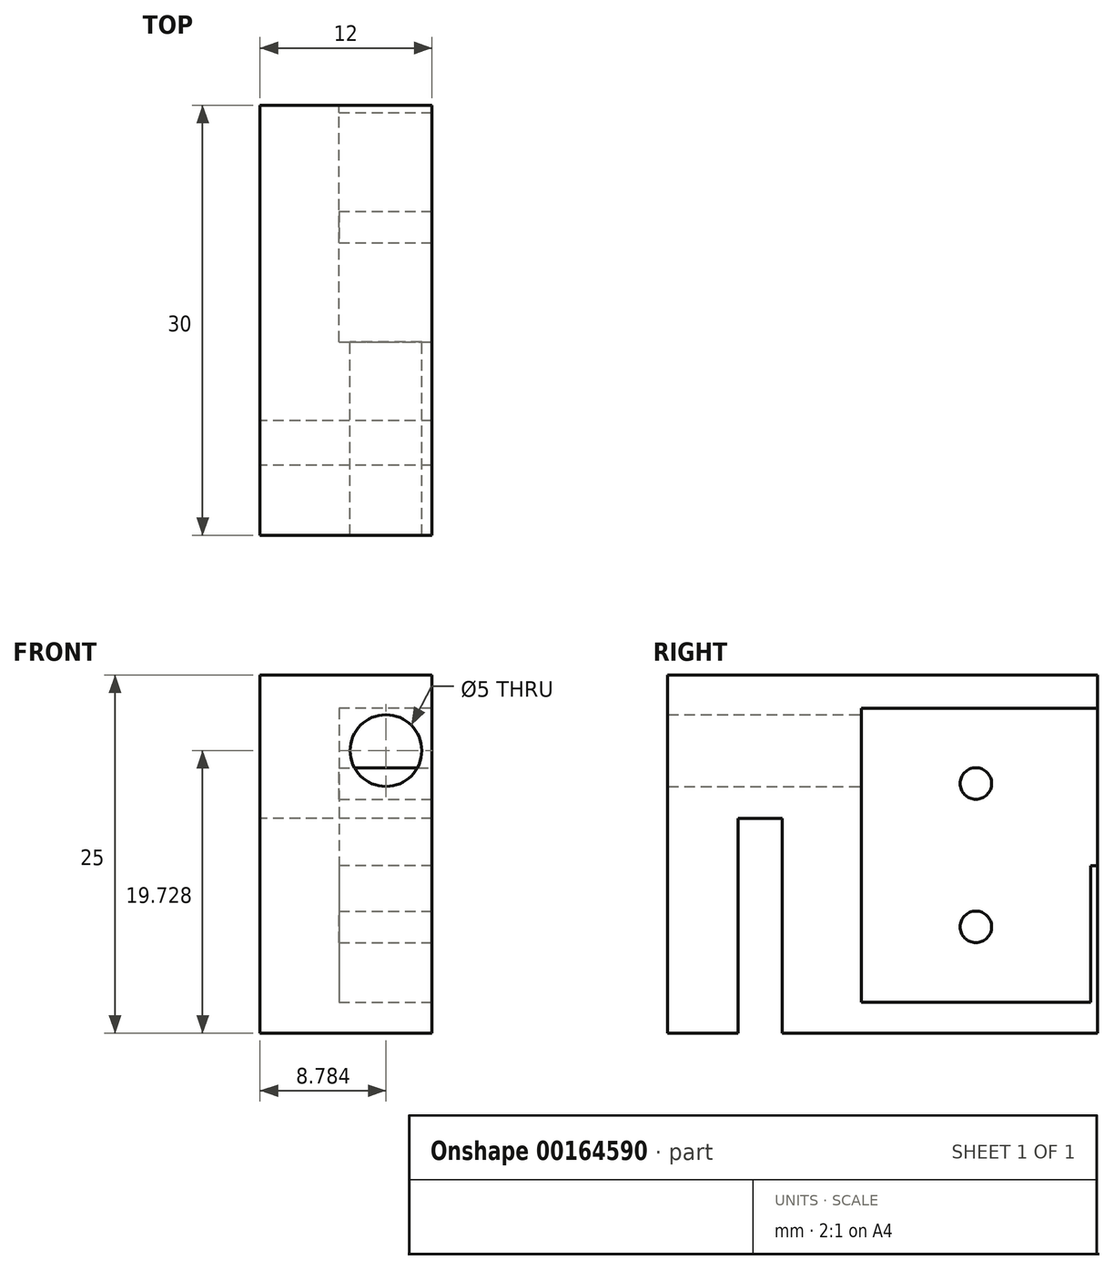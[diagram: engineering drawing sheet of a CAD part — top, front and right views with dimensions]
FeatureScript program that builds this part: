
annotation { "Feature Type Name" : "Feature", "Feature Type Description" : "" }
export const myFeature = defineFeature(function(context is Context, id is Id, definition is map)
    precondition{}
    {
        {
            var Q0;
            Q0=qCreatedBy(makeId("Right.planeOp"),FACE);
            var sketch = newSketch(context, id + "F0", { "sketchPlane" : qUnion([Q0])});
            skLineSegment(sketch, "E0.bottom", {"start": v(-4.9, -0.08) * mm, "end": v(25.1, -0.08) * mm});
            skLineSegment(sketch, "E0.top", {"start": v(-4.9, -25.08) * mm, "end": v(25.1, -25.08) * mm});
            skLineSegment(sketch, "E0.left", {"start": v(-4.9, -0.08) * mm, "end": v(-4.9, -25.08) * mm});
            skLineSegment(sketch, "E0.right", {"start": v(25.1, -0.08) * mm, "end": v(25.1, -25.08) * mm});
            skLineSegment(sketch, "E1.bottom", {"start": v(0, -25.08) * mm, "end": v(3.1, -25.08) * mm});
            skLineSegment(sketch, "E1.top", {"start": v(0, -10.08) * mm, "end": v(3.1, -10.08) * mm});
            skLineSegment(sketch, "E1.left", {"start": v(0, -25.08) * mm, "end": v(0, -10.08) * mm});
            skLineSegment(sketch, "E1.right", {"start": v(3.1, -25.08) * mm, "end": v(3.1, -10.08) * mm});
            skSolve(sketch);
        }
        {
            var Q0;
            Q0=makeQuery(id+"F0.imprint","IMPRINT",FACE,{"disambiguationData":[TD([[makeQuery(id+"F0.imprint","IMPRINT",EDGE,{"derivedFrom":sQuery(id+"F0.wireOp",EDGE,"E0.bottom")}),-1.0]])]});
            extrude(context, id + "F1", {"entities" : qUnion([Q0]), "depth" : 12 * mm});
        }
        {
            var Q0;
            Q0=makeQuery(id+"F1.opExtrude","CAP_FACE",FACE,{"disambiguationData":[OSD([sQuery(id+"F0.wireOp",EDGE,"E0.bottom"),sQuery(id+"F0.wireOp",EDGE,"E0.top"),sQuery(id+"F0.wireOp",EDGE,"E0.left"),sQuery(id+"F0.wireOp",EDGE,"E0.right"),sQuery(id+"F0.wireOp",EDGE,"E1.top"),sQuery(id+"F0.wireOp",EDGE,"E1.left"),sQuery(id+"F0.wireOp",EDGE,"E1.right")])],"isStart":false});
            var sketch = newSketch(context, id + "F2", { "sketchPlane" : qUnion([Q0])});
            skLineSegment(sketch, "E2.bottom", {"start": v(8.6, -2.4) * mm, "end": v(24.6, -2.4) * mm});
            skLineSegment(sketch, "E2.top", {"start": v(8.6, -22.9) * mm, "end": v(24.6, -22.9) * mm});
            skLineSegment(sketch, "E2.left", {"start": v(8.6, -2.4) * mm, "end": v(8.6, -22.9) * mm});
            skLineSegment(sketch, "E2.right", {"start": v(24.6, -13.4) * mm, "end": v(24.6, -22.9) * mm});
            skLineSegment(sketch, "E3.bottom", {"start": v(24.6, -2.4) * mm, "end": v(28.48, -2.4) * mm});
            skLineSegment(sketch, "E3.top", {"start": v(24.6, -13.4) * mm, "end": v(28.48, -13.4) * mm});
            skLineSegment(sketch, "E3.right", {"start": v(28.48, -2.4) * mm, "end": v(28.48, -13.4) * mm});
            skCircle(sketch, "E4", {"center": v(16.6, -7.65) * mm, "radius": 1.1 * mm});
            skCircle(sketch, "E5", {"center": v(16.6, -17.65) * mm, "radius": 1.1 * mm});
            skSolve(sketch);
        }
        {
            var Q0;
            Q0=qSketchRegion(id+"F2",true);
            extrude(context, id + "F3", {"entities" : qUnion([Q0]), "operationType" : NewBodyOperationType.REMOVE, "oppositeDirection" : true, "depth" : 6.5 * mm});
        }
        {
            var Q0;
            Q0=makeQuery(id+"F3.boolean.opBoolean","COPY",FACE,{"derivedFrom":makeQuery(id+"F3.opExtrude","SWEPT_FACE",FACE,{"disambiguationData":[OSD([sQuery(id+"F2.wireOp",EDGE,"E2.left")])]})});
            var sketch = newSketch(context, id + "F4", { "sketchPlane" : qUnion([Q0])});
            skCircle(sketch, "E6", {"center": v(-8.78, -5.35) * mm, "radius": 2.5 * mm});
            skSolve(sketch);
        }
        {
            var Q0;
            Q0=qSketchRegion(id+"F4",true);
            extrude(context, id + "F5", {"entities" : qUnion([Q0]), "operationType" : NewBodyOperationType.REMOVE, "oppositeDirection" : true, "depth" : 25 * mm});
        }
    });
